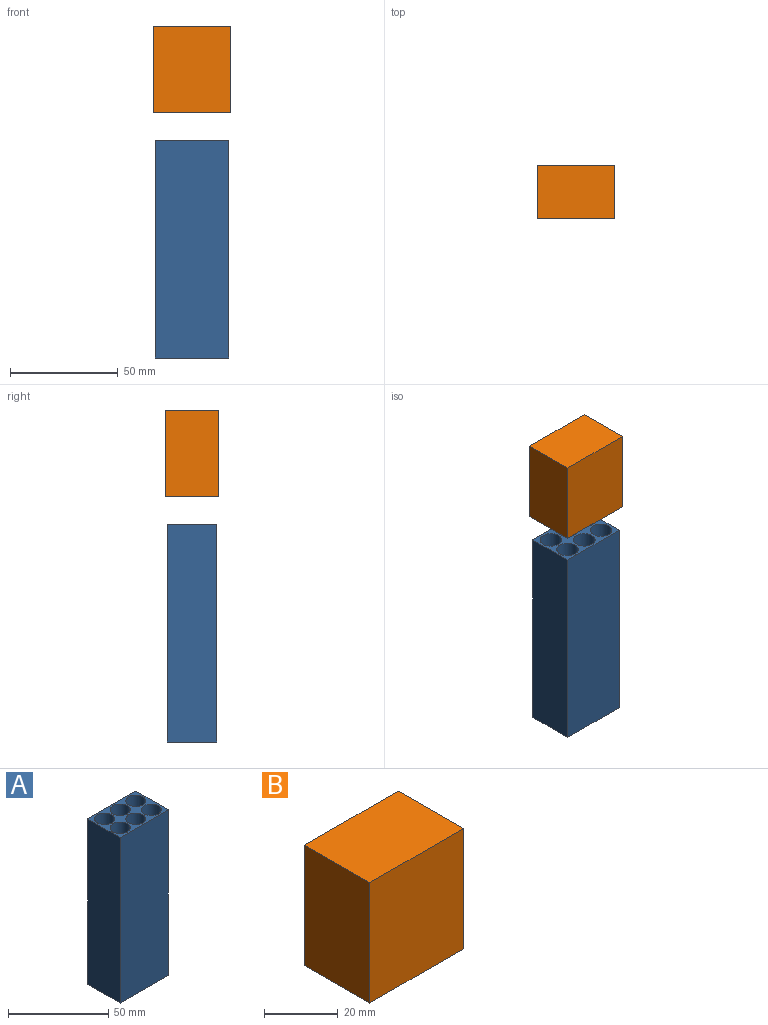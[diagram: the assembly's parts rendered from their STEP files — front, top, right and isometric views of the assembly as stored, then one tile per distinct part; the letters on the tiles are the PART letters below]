
ASSEMBLY  parts=2 mates=1
PART A: 18 faces, bbox 34x23x101 mm
  f0: plane 101x34mm, normal (0,1,0), area 3434mm2, adj f1,f3,f4,f5
  f1: plane 101x23mm, normal (-1,0,0), area 2323mm2, adj f0,f2,f4,f5
  f2: plane 101x34mm, normal (0,-1,0), area 3434mm2, adj f1,f3,f4,f5
  f3: plane 101x23mm, normal (1,0,0), area 2323mm2, adj f0,f2,f4,f5
  f4: plane 34x23mm, normal (0,0,1), area 310.8mm2, adj f0,f1,f2,f3,f6,f8,f10,f12
  f5: plane 34x23mm, normal (0,0,-1), area 782mm2, adj f0,f1,f2,f3
  f6: cylinder r=5mm len=100mm, axis (0,0,1), area 3141.6mm2, adj f4,f7
  f7: plane 10x10mm, normal (0,0,1), area 78.5mm2, adj f6
  f8: cylinder r=5mm len=100mm, axis (0,0,1), area 3141.6mm2, adj f4,f9
  f9: plane 10x10mm, normal (0,0,1), area 78.5mm2, adj f8
  f10: cylinder r=5mm len=100mm, axis (0,0,1), area 3141.6mm2, adj f4,f11
  f11: plane 10x10mm, normal (0,0,1), area 78.5mm2, adj f10
  f12: cylinder r=5mm len=100mm, axis (0,0,1), area 3141.6mm2, adj f4,f13
  f13: plane 10x10mm, normal (0,0,1), area 78.5mm2, adj f12
  f14: cylinder r=5mm len=100mm, axis (0,0,1), area 3141.6mm2, adj f4,f15
  f15: plane 10x10mm, normal (0,0,1), area 78.5mm2, adj f14
  f16: cylinder r=5mm len=100mm, axis (0,0,1), area 3141.6mm2, adj f4,f17
  f17: plane 10x10mm, normal (0,0,1), area 78.5mm2, adj f16
PART B: 11 faces, bbox 36x25x40 mm
  f0: plane 36x25mm, normal (0,0,-1), area 118mm2, adj f1,f2,f3,f4,f6,f7,f8,f9
  f1: plane 40x36mm, normal (0,1,0), area 1440mm2, adj f0,f2,f4,f5
  f2: plane 40x25mm, normal (-1,0,0), area 1000mm2, adj f0,f1,f3,f5
  f3: plane 40x36mm, normal (0,-1,0), area 1440mm2, adj f0,f2,f4,f5
  f4: plane 40x25mm, normal (1,0,0), area 1000mm2, adj f0,f1,f3,f5
  f5: plane 36x25mm, normal (0,0,1), area 900mm2, adj f1,f2,f3,f4
  f6: plane 39x34mm, normal (0,-1,0), area 1326mm2, adj f0,f7,f9,f10
  f7: plane 39x23mm, normal (1,0,0), area 897mm2, adj f0,f6,f8,f10
  f8: plane 39x34mm, normal (0,1,0), area 1326mm2, adj f0,f7,f9,f10
  f9: plane 39x23mm, normal (-1,0,0), area 897mm2, adj f0,f6,f8,f10
  f10: plane 34x23mm, normal (0,0,-1), area 782mm2, adj f6,f7,f8,f9
PLACE A t=(21.57,-4.68,0.6)mm fixed
PLACE B t=(70.14,-10.89,114.96)mm
MATE slider B.f0 <-> A.f4  axis (0,0,1) through (27.11,-10.05,114.96)mm
